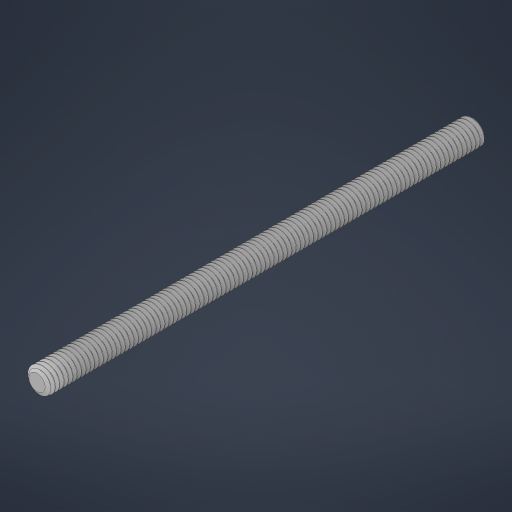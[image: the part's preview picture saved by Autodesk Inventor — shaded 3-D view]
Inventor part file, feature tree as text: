
AUTODESK INVENTOR PART (.ipt)
format: ipt  version: 2023 (Build 270158000, 158)  size: 2,448,896 bytes
history: native  units: in
note: dims shown in document units (in); Inventor stores cm internally (conversion verified against a paired STEP export)
features: mirror x1
ambient origin geometry x8: Origin, YZ Plane, XZ Plane, XY Plane, X Axis, Y Axis, Z Axis, Center Point
bodies: Solid1 (feature_tree)
feature tree (1):
  mirror  "Mirror1"
